# Revit family: Mechanical_Equipment-GE-Zoneline_VTAC-UltimateV12-AirConditioner-Vertical-AZ9V
name_source: partatom
category: Mechanical Equipment
revit_build: Autodesk Revit 2018 (Build: 20190510_1515(x64)
units: mm (PartAtom-declared; Revit-internal decimal feet)

## family parameters
Always vertical = Yes
Cut with Voids When Loaded = No
OmniClass Number = 23.75.70.21.21
OmniClass Title = Local Air-Conditioning Units
Part Type = Normal
Room Calculation Point = No
Round Connector Dimension = Use Diameter
Shared = No
Work Plane-Based = No

## types (2) — shared parameters
Air Supply Diamter = 10"
Apparent Load = 0 VA
Assembly Code = D3040
C Border Thickness = 1"
Depth = 24 1/8"
Description = Vertical Air Conditioner
Frequency = 60 Hz
Height = 31 7/8"
Housing Material = Metal - GE - Sheet Metal
Keynote = 23 30 00
Manufacturer = GE Appliances
Number of Poles = 1
Phase = 1
Power Factor = 1
Product Page URL = https://www.geappliances.com
Return Air Height = 20"
Return Air Width = 20"
URL = https://www.geappliances.com
Version = 2018 v.1.0a
Warranty URL = https://www.geappliances.com
Width = 23 5/8"

## per-type parameters (varying)
| type | Model | Product Name | Voltage |
| 230V-208V_AZ9VH12DBM | AZ9VH12DBM | GE Zoneline® UltimateV12™ Heat Pump Single Package Vertical Air Conditioner with Makeup Air, 230/208 Volt | 230 V |
| 265V_Heat_Pump_With_Backup_Electric_Heat-AZ9VH12EBM | AZ9VH12EBM | GE Zoneline® UltimateV12™ Heat Pump Single Package Vertical Air Conditioner with Makeup Air, 265 Volt | 265 V |

## geometry (parser evidence)
native form markers: Sweep x6
no freeform markers — native parametric forms only
